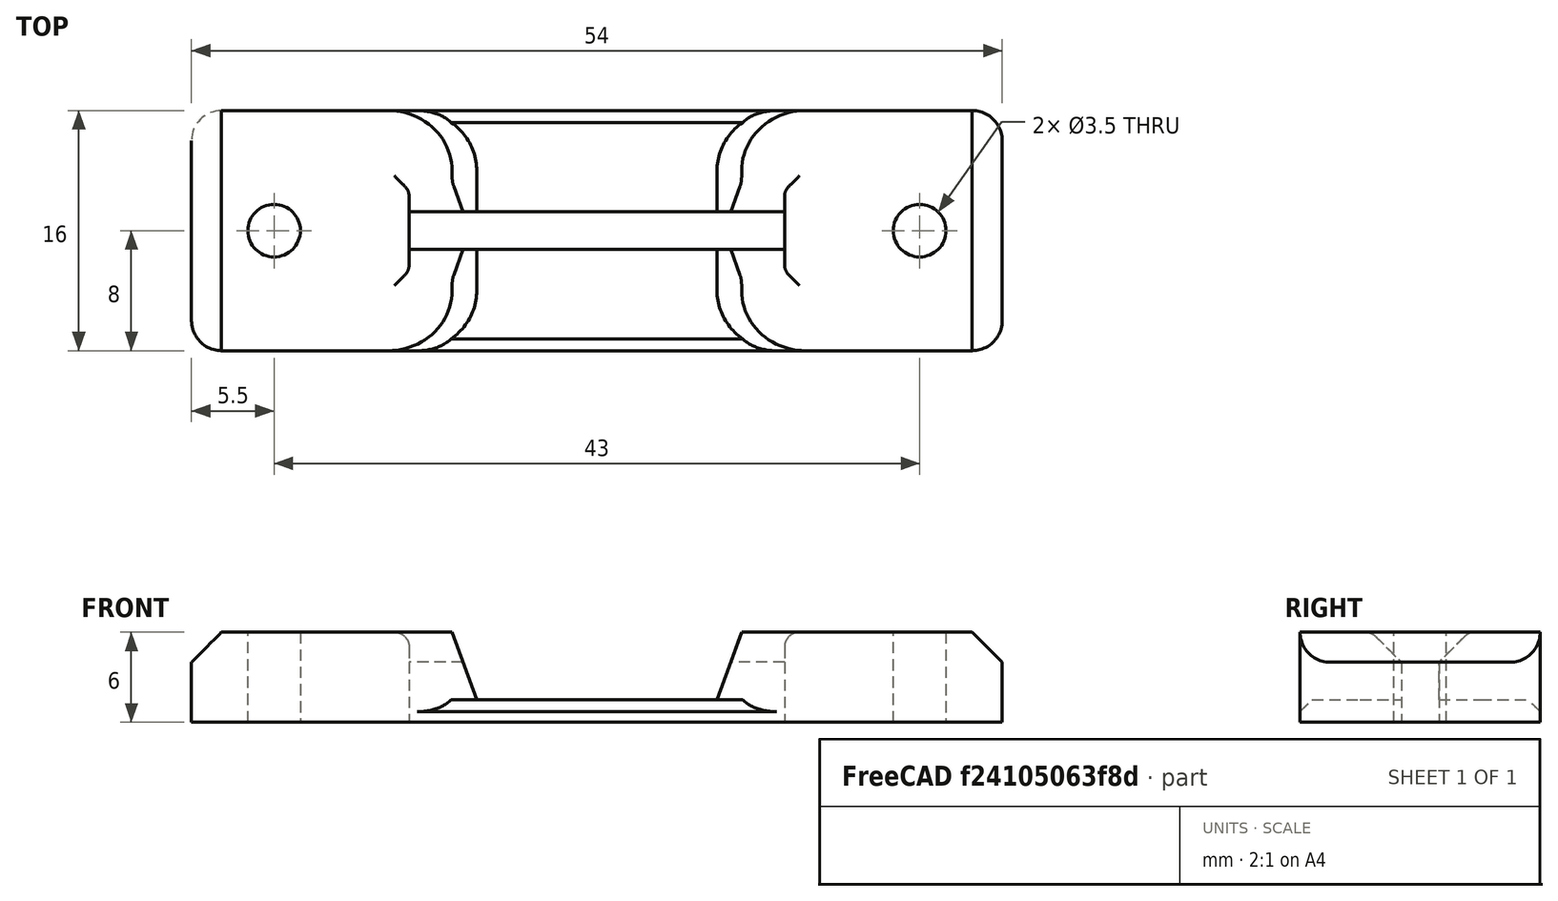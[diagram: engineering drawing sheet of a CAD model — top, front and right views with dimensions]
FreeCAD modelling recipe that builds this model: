
FCSTD DOCUMENT  (FreeCAD 0.19R)
Label: SdGuide
License: All rights reserved
LicenseURL: http://en.wikipedia.org/wiki/All_rights_reserved
objects: PartDesign::Fillet×4, Sketcher::SketchObject×3, PartDesign::Chamfer×3, PartDesign::Pocket×2, PartDesign::Pad×1, PartDesign::Body×1, Mesh::Feature×1
note: 24 computed .brp shape members not serialized (recipe doc carries the construction recipe); baked Part::Feature solids carry a one-line shape summary decoded from their .brp

FEATURE [Sketcher::SketchObject] Sketch
  FullyConstrained = true
  MapMode = 5
  Support = -> [XY_Plane]
  sketch-geometry (4):
    g0: LineSegment StartX=-27 StartY=8 StartZ=0 EndX=27 EndY=8 EndZ=0
    g1: LineSegment StartX=27 StartY=8 StartZ=0 EndX=27 EndY=-8 EndZ=0
    g2: LineSegment StartX=27 StartY=-8 StartZ=0 EndX=-27 EndY=-8 EndZ=0
    g3: LineSegment StartX=-27 StartY=-8 StartZ=0 EndX=-27 EndY=8 EndZ=0
  constraints (11):
    c: Coincident(g0,g1)
    c: Coincident(g1,g2)
    c: Coincident(g2,g3)
    c: Coincident(g3,g0)
    c: Horizontal(g0)
    c: Horizontal(g2)
    c: Vertical(g1)
    c: Vertical(g3)
    c: Symmetric(g1,g0,g-1)
    c: Distance(g0) = 54
    c: Distance(g1) = 16
FEATURE [PartDesign::Pad] Pad
  Direction = (1,1,1)
  Length = 6
  Length2 = 100
  Profile = -> Sketch
  Type = 0
FEATURE [Sketcher::SketchObject] Sketch001
  FullyConstrained = true
  MapMode = 5
  Placement = pos=(0,0,6) rot=(0,0,1;0rad)
  Support = -> [Pad]
  sketch-geometry (6):
    g0: LineSegment StartX=-12.5 StartY=1.25 StartZ=0 EndX=12.5 EndY=1.25 EndZ=0
    g1: LineSegment StartX=12.5 StartY=1.25 StartZ=0 EndX=12.5 EndY=-1.25 EndZ=0
    g2: LineSegment StartX=12.5 StartY=-1.25 StartZ=0 EndX=-12.5 EndY=-1.25 EndZ=0
    g3: LineSegment StartX=-12.5 StartY=-1.25 StartZ=0 EndX=-12.5 EndY=1.25 EndZ=0
    g4: Circle CenterX=-21.5 CenterY=0 CenterZ=0 NormalX=0 NormalY=0 NormalZ=1 AngleXU=0 Radius=1.75
    g5: Circle CenterX=21.5 CenterY=0 CenterZ=0 NormalX=0 NormalY=0 NormalZ=1 AngleXU=0 Radius=1.75
  constraints (16):
    c: Coincident(g0,g1)
    c: Coincident(g1,g2)
    c: Coincident(g2,g3)
    c: Coincident(g3,g0)
    c: Horizontal(g0)
    c: Horizontal(g2)
    c: Vertical(g1)
    c: Vertical(g3)
    c: Distance(g1) = 2.5
    c: Symmetric(g0,g2,g-1)
    c: Distance(g0) = 25
    c: Symmetric(g5,g4,g-1)
    c: PointOnObject(g5,g-1)
    c: Distance(g5,g1) = 9
    c: Diameter(g5) = 3.5
    c: Equal(g5,g4)
FEATURE [PartDesign::Pocket] Pocket
  BaseFeature = -> Pad
  Length = 14
  Length2 = 100
  Profile = -> Sketch001
  Type = 0
FEATURE [Sketcher::SketchObject] Sketch002
  FullyConstrained = false
  MapMode = 5
  Placement = pos=(0,-8,0) rot=(1,0,0;1.5708rad)
  Support = -> [Pocket]
  sketch-geometry (4):
    g0: LineSegment StartX=-8 StartY=1.5 StartZ=0 EndX=8 EndY=1.5 EndZ=0
    g1: LineSegment StartX=8 StartY=1.5 StartZ=0 EndX=11 EndY=9.71405 EndZ=0
    g2: LineSegment StartX=11 StartY=9.71405 StartZ=0 EndX=-11 EndY=9.71405 EndZ=0
    g3: LineSegment StartX=-11 StartY=9.71405 StartZ=0 EndX=-8 EndY=1.5 EndZ=0
  constraints (9):
    c: Coincident(g0,g1)
    c: Coincident(g1,g2)
    c: Coincident(g2,g3)
    c: Coincident(g3,g0)
    c: Symmetric(g0,g0,g-2)
    c: Symmetric(g1,g2,g-2)
    c: Distance(g0) = 16
    c: Distance(g2) = 22
    c: DistanceY(g0) = 1.5
FEATURE [PartDesign::Pocket] Pocket001
  BaseFeature = -> Pocket
  Length = 6.25
  Length2 = 100
  Profile = -> Sketch002
  Type = 1
FEATURE [PartDesign::Chamfer] Chamfer
  Angle = 45
  Base = -> Pocket001 [Edge21,Edge23,Edge38,Edge36]
  BaseFeature = -> Pocket001
  ChamferType = 0
  FlipDirection = false
  Size = 2
  Size2 = 1
  SupportTransform = false
FEATURE [PartDesign::Fillet] Fillet
  Base = -> Chamfer [Edge58,Edge6]
  BaseFeature = -> Chamfer
  Radius = 1
  SupportTransform = false
FEATURE [PartDesign::Fillet] Fillet001
  Base = -> Fillet [Edge2,Edge71,Edge64,Edge11]
  BaseFeature = -> Fillet
  Radius = 1
  SupportTransform = false
FEATURE [PartDesign::Fillet] Fillet002
  Base = -> Fillet001 [Edge41,Edge39,Edge26,Edge20]
  BaseFeature = -> Fillet001
  Radius = 4
  SupportTransform = false
FEATURE [PartDesign::Chamfer] Chamfer001
  Angle = 45
  Base = -> Fillet002 [Edge6,Edge81]
  BaseFeature = -> Fillet002
  ChamferType = 0
  FlipDirection = false
  Size = 2
  Size2 = 1
  SupportTransform = false
FEATURE [PartDesign::Fillet] Fillet003
  Base = -> Chamfer001 [Edge40,Edge20,Edge36,Edge24]
  BaseFeature = -> Chamfer001
  Radius = 2
  SupportTransform = false
FEATURE [PartDesign::Chamfer] Chamfer002
  Angle = 45
  Base = -> Fillet003 [Edge10,Edge79]
  BaseFeature = -> Fillet003
  ChamferType = 0
  FlipDirection = false
  Size = 0.8
  Size2 = 1
  SupportTransform = false
FEATURE [PartDesign::Body] Body
  Group = -> [Sketch,Pad,Sketch001,Pocket,Sketch002,Pocket001,Chamfer,Fillet,Fillet001,Fillet002,Chamfer001,Fillet003,Chamfer002]
  Origin = -> Origin
  Tip = -> Chamfer002
FEATURE [Mesh::Feature] Mesh  label="Chamfer002 (Meshed)"
